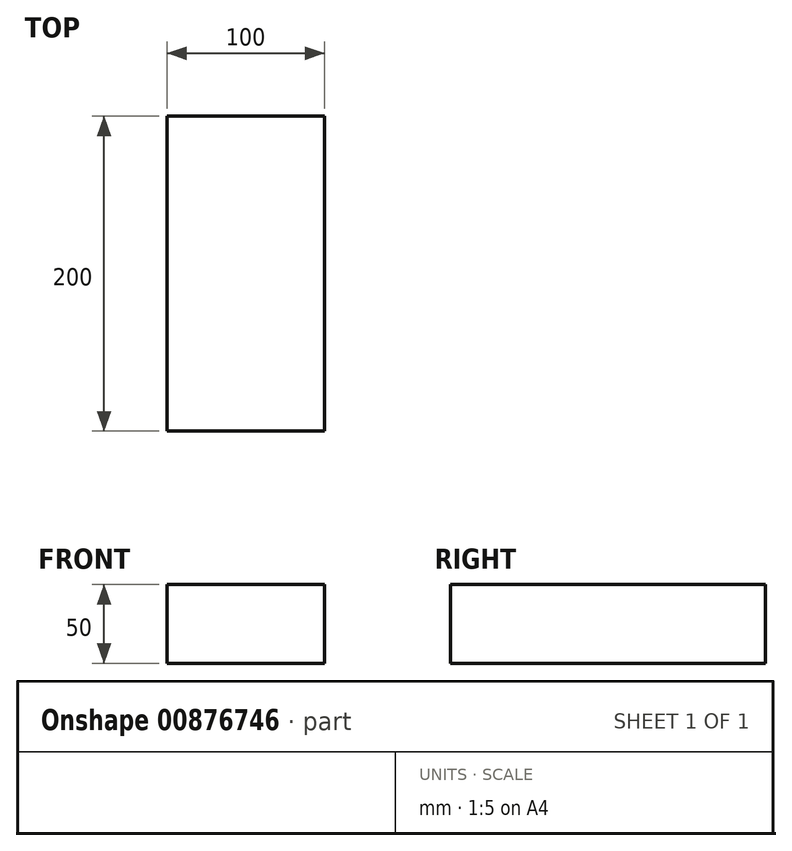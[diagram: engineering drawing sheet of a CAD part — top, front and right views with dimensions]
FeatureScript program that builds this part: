
annotation { "Feature Type Name" : "Feature", "Feature Type Description" : "" }
export const myFeature = defineFeature(function(context is Context, id is Id, definition is map)
    precondition{}
    {
        {
            var Q0;
            Q0=qCreatedBy(makeId("Front.planeOp"),FACE);
            var sketch = newSketch(context, id + "F0", { "sketchPlane" : qUnion([Q0])});
            skLineSegment(sketch, "E0.bottom", {"start": v(-50, 25) * mm, "end": v(50, 25) * mm});
            skLineSegment(sketch, "E0.top", {"start": v(-50, -25) * mm, "end": v(50, -25) * mm});
            skLineSegment(sketch, "E0.left", {"start": v(-50, 25) * mm, "end": v(-50, -25) * mm});
            skLineSegment(sketch, "E0.right", {"start": v(50, 25) * mm, "end": v(50, -25) * mm});
            skLineSegment(sketch, "E1", {"start": v(-50, 25) * mm, "end": v(50, -25) * mm, "construction": true});
            skSolve(sketch);
        }
        {
            var Q0;
            Q0=makeQuery(id+"F0.imprint","IMPRINT",FACE,{"disambiguationData":[TD([[makeQuery(id+"F0.imprint","IMPRINT",EDGE,{"derivedFrom":sQuery(id+"F0.wireOp",EDGE,"E0.bottom")}),-1.0]])]});
            extrude(context, id + "F1", {"entities" : qUnion([Q0]), "depth" : 50 * mm, "offsetDistance" : 25 * mm, "hasSecondDirection" : true, "secondDirectionOppositeDirection" : true, "secondDirectionDepth" : 150 * mm});
        }
        {
            var Q0;
            Q0=makeQuery(id+"F1.opExtrude","SWEPT_FACE",FACE,{"disambiguationData":[OSD([sQuery(id+"F0.wireOp",EDGE,"E0.bottom")])]});
            var sketch = newSketch(context, id + "F2", { "sketchPlane" : qUnion([Q0])});
            skLineSegment(sketch, "E2.0", {"start": v(-50, 41.1) * mm, "end": v(-50, 81.37) * mm});
            skLineSegment(sketch, "E3.0", {"start": v(50, 81.37) * mm, "end": v(50, 150) * mm});
            skLineSegment(sketch, "E4.0.1", {"start": v(-50, 81.37) * mm, "end": v(-50, 41.1) * mm, "construction": true});
            skLineSegment(sketch, "E5", {"start": v(50, 81.37) * mm, "end": v(-50, 41.1) * mm, "construction": true});
            skLineSegment(sketch, "E6", {"start": v(50, 81.37) * mm, "end": v(-50, 81.37) * mm});
            skLineSegment(sketch, "E7", {"start": v(-50, 81.37) * mm, "end": v(-50, 41.1) * mm});
            skPoint(sketch, "E8.orphan", {"position": v(-50, 150) * mm});
            skPoint(sketch, "E9.orphan", {"position": v(-50, -50) * mm});
            skPoint(sketch, "E10.orphan", {"position": v(50, -50) * mm});
            skSolve(sketch);
        }
        {
            var Q0;
            Q0=makeQuery(id+"F1.opExtrude","SWEPT_FACE",FACE,{"disambiguationData":[OSD([sQuery(id+"F0.wireOp",EDGE,"E0.right")])]});
            var sketch = newSketch(context, id + "F3", { "sketchPlane" : qUnion([Q0])});
            skPoint(sketch, "E11.0", {"position": v(81.37, 25) * mm});
            skLineSegment(sketch, "E12", {"start": v(81.37, 25) * mm, "end": v(63.45, -25) * mm, "construction": true});
            skLineSegment(sketch, "E13", {"start": v(81.37, 25) * mm, "end": v(81.37, -25) * mm});
            skLineSegment(sketch, "E14", {"start": v(81.37, -25) * mm, "end": v(63.45, -25) * mm});
            skSolve(sketch);
        }
        {
            var Q0;
            Q0=sQuery(id+"F2.wireOp",EDGE,"E6");
            var Q1;
            Q1=sQuery(id+"F2.wireOp",EDGE,"E2.0");
            var Q2;
            Q2=sQuery(id+"F2.wireOp",EDGE,"E5");
            revolve(context, id + "F4", {"bodyType" : ToolBodyType.SURFACE, "operationType" : NewBodyOperationType.ADD, "surfaceOperationType" : NewSurfaceOperationType.NEW, "surfaceEntities" : qUnion([Q0, Q1]), "axis" : qUnion([Q2]), "revolveType" : RevolveType.FULL});
        }
        {
            var Q0;
            Q0=sQuery(id+"F3.wireOp",EDGE,"E13");
            var Q1;
            Q1=sQuery(id+"F3.wireOp",EDGE,"E14");
            var Q2;
            Q2=sQuery(id+"F3.wireOp",EDGE,"E12");
            revolve(context, id + "F5", {"bodyType" : ToolBodyType.SURFACE, "surfaceOperationType" : NewSurfaceOperationType.NEW, "surfaceEntities" : qUnion([Q0, Q1]), "axis" : qUnion([Q2]), "revolveType" : RevolveType.FULL});
        }
        {
            var Q0;
            Q0=makeQuery(id+"F1.opExtrude","SWEPT_FACE",FACE,{"disambiguationData":[OSD([sQuery(id+"F0.wireOp",EDGE,"E0.bottom")])]});
            var sketch = newSketch(context, id + "F6", { "sketchPlane" : qUnion([Q0])});
            skPoint(sketch, "E15.0", {"position": v(50, 81.37) * mm});
            skPoint(sketch, "E16.0", {"position": v(-50, 41.1) * mm});
            skLineSegment(sketch, "E17", {"start": v(50, 81.37) * mm, "end": v(-50, 41.1) * mm});
            skSolve(sketch);
        }
        {
            var Q0;
            Q0=makeQuery(id+"F1.opExtrude","SWEPT_FACE",FACE,{"disambiguationData":[OSD([sQuery(id+"F0.wireOp",EDGE,"E0.right")])]});
            var sketch = newSketch(context, id + "F7", { "sketchPlane" : qUnion([Q0])});
            skPoint(sketch, "E18.0", {"position": v(81.37, 25) * mm});
            skPoint(sketch, "E18.1", {"position": v(63.45, -25) * mm});
            skLineSegment(sketch, "E19", {"start": v(81.37, 25) * mm, "end": v(63.45, -25) * mm});
            skSolve(sketch);
        }
        {
            var Q0;
            {var subQ0=sQuery(id+"F6.wireOp",EDGE,"E17");Q0=makeQuery(id+"F6.imprint","IMPRINT",FACE,{"disambiguationData":[TD([[makeQuery(id+"F6.imprint","IMPRINT",EDGE,{"derivedFrom":subQ0}),-1.0]])]});}
            var sketch = newSketch(context, id + "F8", { "sketchPlane" : qUnion([Q0])});
            skPoint(sketch, "E20.0", {"position": v(50, 81.37) * mm});
            skPoint(sketch, "E21.orphan", {"position": v(-50, 150) * mm});
            skPoint(sketch, "E22.1.start.orphan", {"position": v(-50, -50) * mm});
            skPoint(sketch, "E22.0.end.orphan", {"position": v(-50, 81.37) * mm});
            skPoint(sketch, "E22.0.start.orphan", {"position": v(-22.1, 12.08) * mm});
            skLineSegment(sketch, "E23", {"start": v(-50, 81.37) * mm, "end": v(50, 81.37) * mm});
            skSolve(sketch);
        }
        {
            var Q0;
            {var subQ0=sQuery(id+"F7.wireOp",EDGE,"E19");Q0=makeQuery(id+"F7.imprint","IMPRINT",FACE,{"disambiguationData":[TD([[makeQuery(id+"F7.imprint","IMPRINT",EDGE,{"derivedFrom":subQ0}),1.0]])]});}
            var sketch = newSketch(context, id + "F9", { "sketchPlane" : qUnion([Q0])});
            skPoint(sketch, "E24.0.end.orphan", {"position": v(49.62, -13.62) * mm});
            skPoint(sketch, "E24.0.start.orphan", {"position": v(81.37, -25) * mm});
            skPoint(sketch, "E25.0", {"position": v(81.37, 25) * mm});
            skLineSegment(sketch, "E26", {"start": v(81.37, 25) * mm, "end": v(81.37, -25) * mm});
            skSolve(sketch);
        }
        {
            var Q0;
            Q0=sQuery(id+"F8.wireOp",VERTEX,"E22.0.end.orphan");
            var Q1;
            Q1=makeQuery(id+"F4.opRevolve","SWEPT_EDGE",EDGE,{"disambiguationData":[OSD([sQuery(id+"F2.wireOp",VERTEX,"E2.0.end")])]});
            cPlane(context, id + "F10", {"entities" : qUnion([Q0, Q1]), "cplaneType" : CPlaneType.LINE_POINT, "offset" : 25 * mm, "width" : 150 * mm, "height" : 150 * mm});
        }
        {
            var Q0;
            Q0=qCreatedBy(id+"F10.planeOp",FACE);
            var sketch = newSketch(context, id + "F11", { "sketchPlane" : qUnion([Q0])});
            skCircle(sketch, "E27.0", {"center": v(-56.8, 25) * mm, "radius": 37.35 * mm, "construction": true});
            skPoint(sketch, "E28.0", {"position": v(-40.19, -25) * mm});
            skLineSegment(sketch, "E29", {"start": v(-40.19, -25) * mm, "end": v(-56.8, 25) * mm, "construction": true});
            skPoint(sketch, "E30", {"position": v(-26.89, 47.36) * mm});
            skSolve(sketch);
        }
        {
            var Q0;
            Q0=sQuery(id+"F6.wireOp",VERTEX,"E15.0");
            var Q1;
            Q1=sQuery(id+"F11.wireOp",VERTEX,"E30");
            var Q2;
            Q2=sQuery(id+"F6.wireOp",VERTEX,"E16.0");
            cPlane(context, id + "F12", {"entities" : qUnion([Q0, Q1, Q2]), "cplaneType" : CPlaneType.THREE_POINT, "offset" : 25 * mm, "width" : 150 * mm, "height" : 150 * mm});
        }
        {
            var Q0;
            Q0=qCreatedBy(id+"F12.planeOp",FACE);
            var sketch = newSketch(context, id + "F13", { "sketchPlane" : qUnion([Q0])});
            skPoint(sketch, "E31.0", {"position": v(63.7, 52.63) * mm});
            skPoint(sketch, "E32.0", {"position": v(-13.13, -11.39) * mm});
            skPoint(sketch, "E33.0", {"position": v(-38.9, 19.54) * mm});
            skLineSegment(sketch, "E34", {"start": v(63.7, 52.63) * mm, "end": v(-38.9, 19.54) * mm});
            skLineSegment(sketch, "E35", {"start": v(-13.13, -11.39) * mm, "end": v(63.7, 52.63) * mm});
            skLineSegment(sketch, "E36", {"start": v(-13.13, -11.39) * mm, "end": v(-38.9, 19.54) * mm});
            skSolve(sketch);
        }
        {
            var Q0;
            Q0=makeQuery(id+"F5.opRevolve","SWEPT_EDGE",EDGE,{"disambiguationData":[OSD([sQuery(id+"F3.wireOp",VERTEX,"E14.start")])]});
            var Q1;
            Q1=sQuery(id+"F9.wireOp",VERTEX,"E24.0.start.orphan");
            cPlane(context, id + "F14", {"entities" : qUnion([Q0, Q1]), "cplaneType" : CPlaneType.LINE_POINT, "offset" : 25 * mm, "width" : 150 * mm, "height" : 150 * mm});
        }
        {
            var Q0;
            Q0=qCreatedBy(id+"F14.planeOp",FACE);
            var sketch = newSketch(context, id + "F15", { "sketchPlane" : qUnion([Q0])});
            skLineSegment(sketch, "E37.1", {"start": v(50, -68.17) * mm, "end": v(-50, -30.27) * mm});
            skLineSegment(sketch, "E38.1", {"start": v(50, -68.17) * mm, "end": v(-50, -30.27) * mm, "construction": true});
            skCircle(sketch, "E39.0", {"center": v(50, -68.17) * mm, "radius": 16.86 * mm, "construction": true});
            skPoint(sketch, "E40", {"position": v(61.18, -55.54) * mm});
            skSolve(sketch);
        }
        {
            var Q0;
            Q0=sQuery(id+"F6.wireOp",VERTEX,"E15.0");
            var Q1;
            Q1=sQuery(id+"F15.wireOp",VERTEX,"E40");
            var Q2;
            Q2=sQuery(id+"F7.wireOp",VERTEX,"E18.1");
            cPlane(context, id + "F16", {"entities" : qUnion([Q0, Q1, Q2]), "cplaneType" : CPlaneType.THREE_POINT, "offset" : 25 * mm, "width" : 150 * mm, "height" : 150 * mm});
        }
        {
            var Q0;
            Q0=qCreatedBy(id+"F16.planeOp",FACE);
            var sketch = newSketch(context, id + "F17", { "sketchPlane" : qUnion([Q0])});
            skPoint(sketch, "E41.0", {"position": v(-38.15, 38.26) * mm});
            skPoint(sketch, "E42.0", {"position": v(-15.23, -9.65) * mm});
            skPoint(sketch, "E43.0", {"position": v(-2.62, 3.08) * mm});
            skLineSegment(sketch, "E44", {"start": v(-2.62, 3.08) * mm, "end": v(-38.15, 38.26) * mm});
            skLineSegment(sketch, "E45", {"start": v(-15.23, -9.65) * mm, "end": v(-2.62, 3.08) * mm});
            skLineSegment(sketch, "E46", {"start": v(-38.15, 38.26) * mm, "end": v(-15.23, -9.65) * mm});
            skSolve(sketch);
        }
        {
            var Q0;
            Q0=sQuery(id+"F8.wireOp",VERTEX,"E22.0.end.orphan");
            var Q1;
            Q1=sQuery(id+"F8.wireOp",VERTEX,"E20.0");
            var Q2;
            Q2=sQuery(id+"F9.wireOp",VERTEX,"E24.0.start.orphan");
            cPlane(context, id + "F18", {"entities" : qUnion([Q0, Q1, Q2]), "cplaneType" : CPlaneType.THREE_POINT, "offset" : 25 * mm, "width" : 150 * mm, "height" : 150 * mm});
        }
        {
            var Q0;
            Q0=sQuery(id+"F13.wireOp",VERTEX,"E32.0");
            var Q1;
            Q1=sQuery(id+"F8.wireOp",VERTEX,"E20.0");
            var Q2;
            Q2=sQuery(id+"F17.wireOp",VERTEX,"E43.0");
            cPlane(context, id + "F19", {"entities" : qUnion([Q0, Q1, Q2]), "cplaneType" : CPlaneType.THREE_POINT, "offset" : 25 * mm, "width" : 150 * mm, "height" : 150 * mm});
        }
        {
            var Q0;
            Q0=sQuery(id+"F13.wireOp",VERTEX,"E33.0");
            var Q1;
            Q1=sQuery(id+"F8.wireOp",VERTEX,"E20.0");
            var Q2;
            Q2=sQuery(id+"F17.wireOp",VERTEX,"E42.0");
            cPlane(context, id + "F20", {"entities" : qUnion([Q0, Q1, Q2]), "cplaneType" : CPlaneType.THREE_POINT, "offset" : 25 * mm, "width" : 150 * mm, "height" : 150 * mm});
        }
        {
            var Q0;
            Q0=sQuery(id+"F8.wireOp",VERTEX,"E22.0.end.orphan");
            var Q1;
            Q1=sQuery(id+"F13.wireOp",VERTEX,"E33.0");
            var Q2;
            Q2=sQuery(id+"F8.wireOp",VERTEX,"E20.0");
            cPlane(context, id + "F21", {"entities" : qUnion([Q0, Q1, Q2]), "cplaneType" : CPlaneType.THREE_POINT, "offset" : 25 * mm, "width" : 150 * mm, "height" : 150 * mm});
        }
        {
            var Q0;
            Q0=sQuery(id+"F8.wireOp",VERTEX,"E20.0");
            var Q1;
            Q1=sQuery(id+"F9.wireOp",VERTEX,"E24.0.start.orphan");
            var Q2;
            Q2=sQuery(id+"F17.wireOp",VERTEX,"E42.0");
            cPlane(context, id + "F22", {"entities" : qUnion([Q0, Q1, Q2]), "cplaneType" : CPlaneType.THREE_POINT, "offset" : 25 * mm, "width" : 150 * mm, "height" : 150 * mm});
        }
    });
